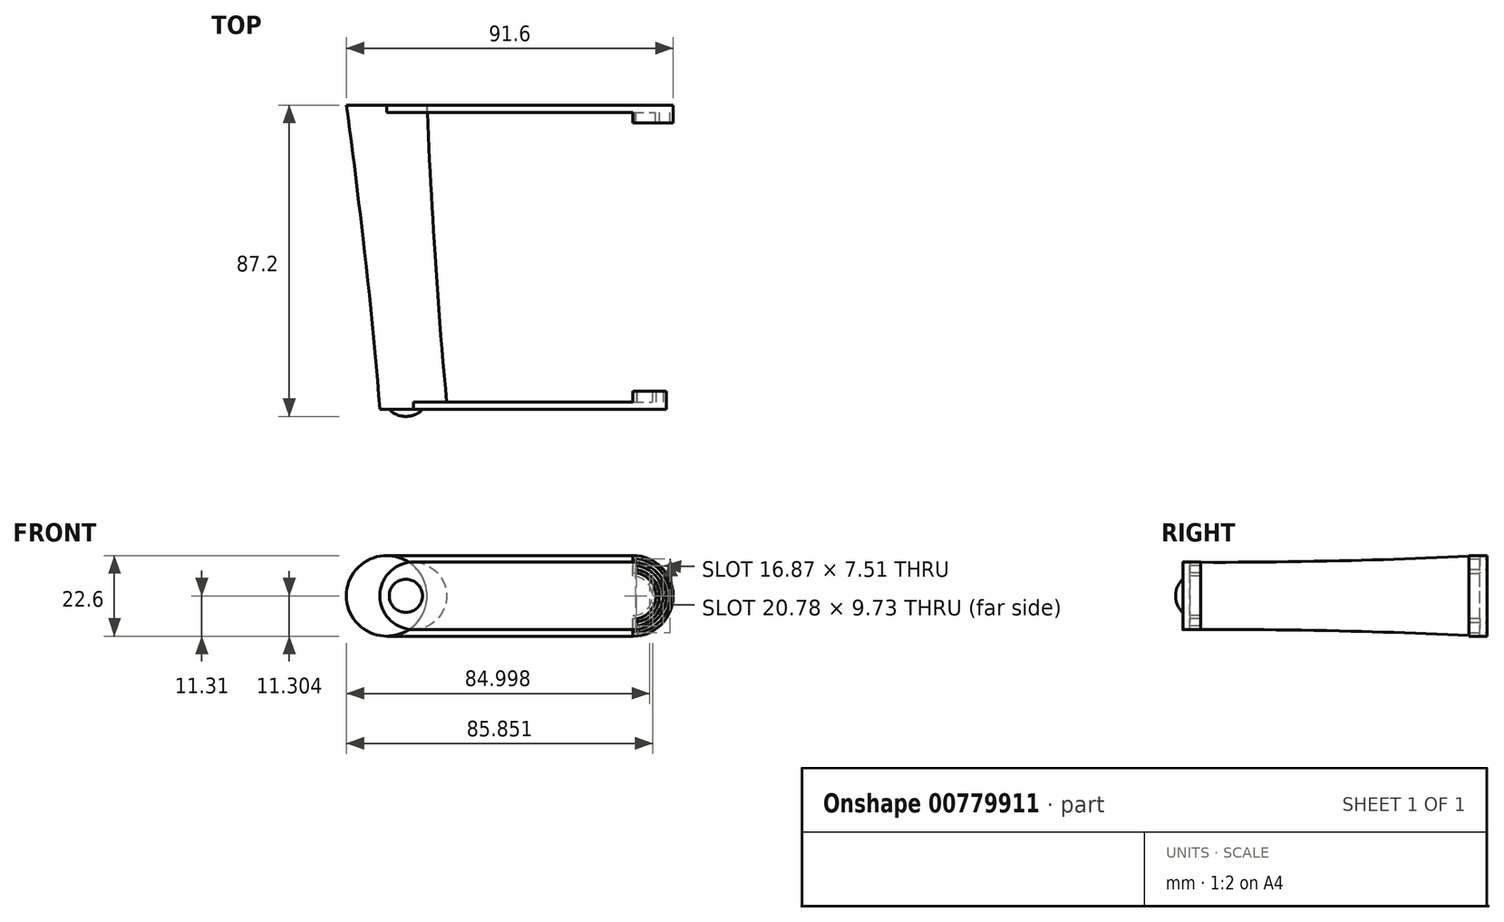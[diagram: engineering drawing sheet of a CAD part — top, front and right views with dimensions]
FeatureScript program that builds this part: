
annotation { "Feature Type Name" : "Feature", "Feature Type Description" : "" }
export const myFeature = defineFeature(function(context is Context, id is Id, definition is map)
    precondition{}
    {
        {
            var Q0;
            Q0=qCreatedBy(makeId("Front.planeOp"),FACE);
            var sketch = newSketch(context, id + "F0", { "sketchPlane" : qUnion([Q0])});
            skCircle(sketch, "E0", {"center": v(0, 0) * mm, "radius": 11.3 * mm});
            skLineSegment(sketch, "E1", {"start": v(0, 11.3) * mm, "end": v(69, 11.3) * mm});
            skLineSegment(sketch, "E2", {"start": v(0, -11.3) * mm, "end": v(69, -11.3) * mm});
            skLineSegment(sketch, "E3", {"start": v(69, 11.3) * mm, "end": v(69, 6.3) * mm});
            skLineSegment(sketch, "E4", {"start": v(69, -6.3) * mm, "end": v(69, -11.3) * mm});
            skArc(sketch, "E5", {"start": v(69, -11.3) * mm, "mid": v(80.3, 0) * mm, "end": v(69, 11.3) * mm});
            skArc(sketch, "E6", {"start": v(69, -6.3) * mm, "mid": v(75.3, 0) * mm, "end": v(69, 6.3) * mm});
            skArc(sketch, "E7", {"start": v(69.69, 10.4) * mm, "mid": v(79.41, 0.06) * mm, "end": v(69.8, -10.38) * mm});
            skArc(sketch, "E8", {"start": v(69.69, 7.4) * mm, "mid": v(76.42, 0.05) * mm, "end": v(69.78, -7.38) * mm});
            skLineSegment(sketch, "E9", {"start": v(69.69, 10.4) * mm, "end": v(69.69, 7.4) * mm});
            skLineSegment(sketch, "E10", {"start": v(69.78, -7.38) * mm, "end": v(69.8, -10.38) * mm});
            skSolve(sketch);
        }
        {
            var Q0;
            Q0=qCreatedBy(makeId("Front.planeOp"),FACE);
            cPlane(context, id + "F1", {"entities" : qUnion([Q0]), "cplaneType" : CPlaneType.OFFSET, "offset" : 85.2 * mm, "width" : 150 * mm, "height" : 150 * mm});
        }
        {
            var Q0;
            Q0=qCreatedBy(id+"F1.planeOp",FACE);
            var sketch = newSketch(context, id + "F2", { "sketchPlane" : qUnion([Q0])});
            skCircle(sketch, "E11", {"center": v(7.55, 0) * mm, "radius": 9.45 * mm});
            skSolve(sketch);
        }
        {
            var Q0;
            Q0=makeQuery(id+"F2.imprint","IMPRINT",FACE,{"disambiguationData":[TD([[makeQuery(id+"F2.imprint","IMPRINT",EDGE,{"derivedFrom":sQuery(id+"F2.wireOp",EDGE,"E11")}),1.0]])]});
            var Q1;
            {var subQ0=sQuery(id+"F0.wireOp",EDGE,"E0");var subQ1=makeQuery(id+"F0.imprint","INTERSECT",VERTEX,{"derivedFrom":[subQ0,sQuery(id+"F0.wireOp",EDGE,"E1")]});Q1=makeQuery(id+"F0.imprint","IMPRINT",FACE,{"disambiguationData":[TD([[makeQuery(id+"F0.imprint","IMPRINT",EDGE,{"disambiguationData":[TD([[subQ1,-1.0]])],"derivedFrom":subQ0}),1.0]])]});}
            loft(context, id + "F3", {"sheetProfilesArray" : [{ "sheetProfileEntities" : qUnion([Q0]) }, { "sheetProfileEntities" : qUnion([Q1]) }]});
        }
        {
            var Q0;
            {var subQ1=sQuery(id+"F0.wireOp",EDGE,"E1");Q0=makeQuery(id+"F0.imprint","IMPRINT",FACE,{"disambiguationData":[TD([[makeQuery(id+"F0.imprint","IMPRINT",EDGE,{"derivedFrom":subQ1}),-1.0]])]});}
            var Q1;
            Q1=qSketchRegion(id+"F6",true);
            extrude(context, id + "F4", {"entities" : qUnion([Q0, Q1]), "depth" : 2 * mm, "offsetDistance" : 25 * mm});
        }
        {
            var Q0;
            Q0=makeQuery(id+"F0.imprint","IMPRINT",FACE,{"disambiguationData":[TD([[makeQuery(id+"F0.imprint","IMPRINT",EDGE,{"derivedFrom":sQuery(id+"F0.wireOp",EDGE,"E3")}),1.0]])]});
            extrude(context, id + "F5", {"entities" : qUnion([Q0]), "operationType" : NewBodyOperationType.ADD, "depth" : 5 * mm, "offsetDistance" : 25 * mm});
        }
        {
            var Q0;
            Q0=qCreatedBy(id+"F1.planeOp",FACE);
            var sketch = newSketch(context, id + "F6", { "sketchPlane" : qUnion([Q0])});
            skLineSegment(sketch, "E12.bottom", {"start": v(7.55, -9.45) * mm, "end": v(68.95, -9.45) * mm});
            skLineSegment(sketch, "E12.top", {"start": v(7.55, 9.45) * mm, "end": v(68.95, 9.45) * mm});
            skLineSegment(sketch, "E12.left", {"start": v(7.55, -9.45) * mm, "end": v(7.55, 9.45) * mm});
            skLineSegment(sketch, "E12.right", {"start": v(68.95, -9.45) * mm, "end": v(68.95, 9.45) * mm});
            skArc(sketch, "E13", {"start": v(68.95, -9.45) * mm, "mid": v(78.4, 0) * mm, "end": v(68.95, 9.45) * mm});
            skArc(sketch, "E14", {"start": v(68.95, -5.5) * mm, "mid": v(74.45, 0) * mm, "end": v(68.95, 5.5) * mm});
            skArc(sketch, "E15", {"start": v(69.94, 8.44) * mm, "mid": v(77.46, 0.08) * mm, "end": v(70.1, -8.42) * mm});
            skArc(sketch, "E16", {"start": v(69.94, 6.44) * mm, "mid": v(75.47, 0.08) * mm, "end": v(70.1, -6.42) * mm});
            skLineSegment(sketch, "E17", {"start": v(69.94, 8.44) * mm, "end": v(69.94, 6.44) * mm});
            skLineSegment(sketch, "E18", {"start": v(70.1, -6.42) * mm, "end": v(70.1, -8.42) * mm});
            skSolve(sketch);
        }
        {
            var Q0;
            Q0=makeQuery(id+"F6.imprint","IMPRINT",FACE,{"disambiguationData":[TD([[makeQuery(id+"F6.imprint","IMPRINT",EDGE,{"derivedFrom":sQuery(id+"F6.wireOp",EDGE,"E12.bottom")}),1.0]])]});
            extrude(context, id + "F7", {"entities" : qUnion([Q0]), "operationType" : NewBodyOperationType.ADD, "oppositeDirection" : true, "depth" : 2 * mm, "offsetDistance" : 25 * mm});
        }
        {
            var Q0;
            Q0=makeQuery(id+"F6.imprint","IMPRINT",FACE,{"disambiguationData":[TD([[makeQuery(id+"F6.imprint","IMPRINT",EDGE,{"derivedFrom":sQuery(id+"F6.wireOp",EDGE,"E12.right")}),-1.0]])]});
            extrude(context, id + "F8", {"entities" : qUnion([Q0]), "operationType" : NewBodyOperationType.ADD, "oppositeDirection" : true, "depth" : 5 * mm, "offsetDistance" : 25 * mm});
        }
        {
            var Q0;
            Q0=qCreatedBy(id+"F1.planeOp",FACE);
            var sketch = newSketch(context, id + "F9", { "sketchPlane" : qUnion([Q0])});
            skCircle(sketch, "E19", {"center": v(5.37, 0) * mm, "radius": 4.65 * mm});
            skSolve(sketch);
        }
        {
            var Q0;
            Q0=qSketchRegion(id+"F9",true);
            extrude(context, id + "F10", {"entities" : qUnion([Q0]), "operationType" : NewBodyOperationType.ADD, "depth" : 2 * mm, "offsetDistance" : 25 * mm});
        }
        {
            var Q0;
            Q0=makeQuery(id+"F10.opExtrude","CAP_FACE",FACE,{"disambiguationData":[OSD([sQuery(id+"F9.wireOp",EDGE,"E19")])],"isStart":false});
            fillet(context, id + "F11", {"entities" : qUnion([Q0]), "radius" : 6 * mm, "tangentPropagation" : true, "allowEdgeOverflow" : false});
        }
        {
            var Q0;
            {var subQ0=sQuery(id+"F6.wireOp",EDGE,"E14");Q0=makeQuery(id+"F6.imprint","IMPRINT",FACE,{"disambiguationData":[TD([[makeQuery(id+"F6.imprint","IMPRINT",EDGE,{"derivedFrom":subQ0}),1.0]])]});}
            extrude(context, id + "F12", {"entities" : qUnion([Q0]), "operationType" : NewBodyOperationType.ADD, "oppositeDirection" : true, "depth" : 2 * mm, "offsetDistance" : 25 * mm});
        }
        {
            var Q0;
            Q0=makeQuery(id+"F0.imprint","IMPRINT",FACE,{"disambiguationData":[TD([[makeQuery(id+"F0.imprint","IMPRINT",EDGE,{"derivedFrom":sQuery(id+"F0.wireOp",EDGE,"E7")}),-1.0]])]});
            extrude(context, id + "F13", {"entities" : qUnion([Q0]), "operationType" : NewBodyOperationType.ADD, "depth" : 2 * mm, "offsetDistance" : 25 * mm});
        }
        {
            var Q0;
            Q0=makeQuery(id+"F0.imprint","IMPRINT",FACE,{"disambiguationData":[TD([[makeQuery(id+"F0.imprint","IMPRINT",EDGE,{"derivedFrom":sQuery(id+"F0.wireOp",EDGE,"E7")}),-1.0]])]});
            extrude(context, id + "F14", {"entities" : qUnion([Q0]), "operationType" : NewBodyOperationType.ADD, "depth" : 3 * mm, "offsetDistance" : 25 * mm});
        }
        {
            var Q0;
            Q0=makeQuery(id+"F6.imprint","IMPRINT",FACE,{"disambiguationData":[TD([[makeQuery(id+"F6.imprint","IMPRINT",EDGE,{"derivedFrom":sQuery(id+"F6.wireOp",EDGE,"E15")}),-1.0]])]});
            extrude(context, id + "F15", {"entities" : qUnion([Q0]), "operationType" : NewBodyOperationType.ADD, "oppositeDirection" : true, "depth" : 2 * mm, "offsetDistance" : 25 * mm});
        }
    });
